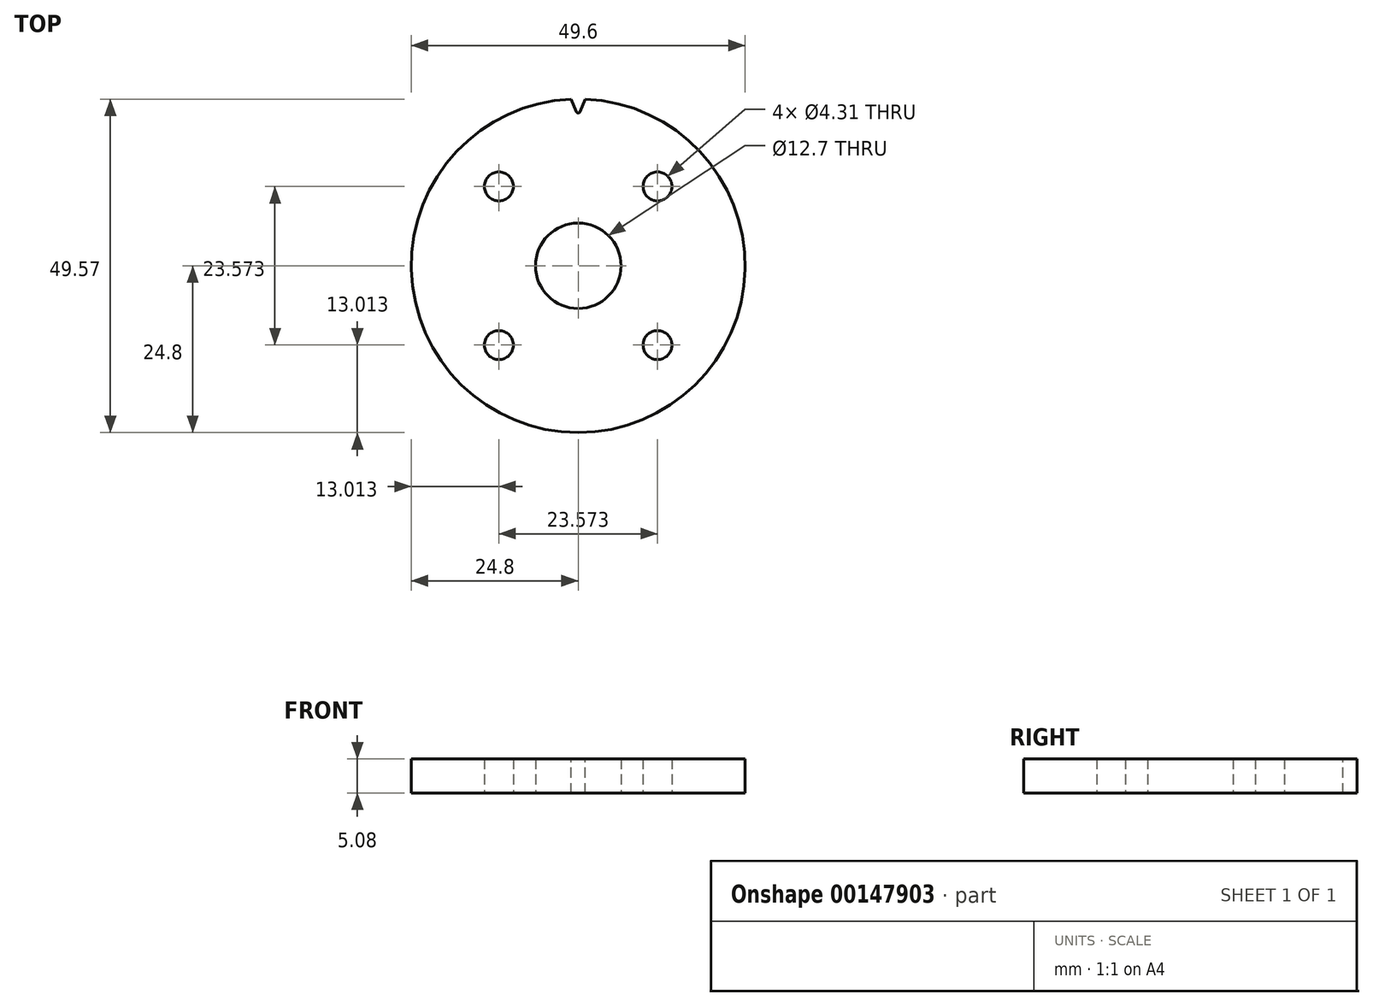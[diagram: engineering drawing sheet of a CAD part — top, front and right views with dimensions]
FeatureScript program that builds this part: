
annotation { "Feature Type Name" : "Feature", "Feature Type Description" : "" }
export const myFeature = defineFeature(function(context is Context, id is Id, definition is map)
    precondition{}
    {
        {
            var Q0;
            Q0=qCreatedBy(makeId("Top.planeOp"),FACE);
            var sketch = newSketch(context, id + "F0", { "sketchPlane" : qUnion([Q0])});
            skCircle(sketch, "E0", {"center": v(0, 0) * mm, "radius": 24.8 * mm});
            skCircle(sketch, "E1", {"center": v(0, 0) * mm, "radius": 11.11 * mm, "construction": true});
            skLineSegment(sketch, "E2.bottom", {"start": v(11.79, 11.79) * mm, "end": v(-11.79, 11.79) * mm, "construction": true});
            skLineSegment(sketch, "E2.top", {"start": v(11.79, -11.79) * mm, "end": v(-11.79, -11.79) * mm, "construction": true});
            skLineSegment(sketch, "E2.left", {"start": v(11.79, 11.79) * mm, "end": v(11.79, -11.79) * mm, "construction": true});
            skLineSegment(sketch, "E2.right", {"start": v(-11.79, 11.79) * mm, "end": v(-11.79, -11.79) * mm, "construction": true});
            skCircle(sketch, "E3", {"center": v(11.79, 11.79) * mm, "radius": 5.56 * mm, "construction": true});
            skCircle(sketch, "E4", {"center": v(-11.79, 11.79) * mm, "radius": 2.15 * mm});
            skCircle(sketch, "E5", {"center": v(11.79, 11.79) * mm, "radius": 2.15 * mm});
            skCircle(sketch, "E6", {"center": v(11.79, -11.79) * mm, "radius": 2.15 * mm});
            skCircle(sketch, "E7", {"center": v(-11.79, -11.79) * mm, "radius": 2.15 * mm});
            skCircle(sketch, "E8", {"center": v(0, 0) * mm, "radius": 6.35 * mm});
            skSolve(sketch);
        }
        {
            var Q0;
            Q0=makeQuery(id+"F0.imprint","IMPRINT",FACE,{"disambiguationData":[TD([[makeQuery(id+"F0.imprint","IMPRINT",EDGE,{"derivedFrom":sQuery(id+"F0.wireOp",EDGE,"d7zeTPih-CRss-xDOh-gPdP-rmPCdwzH7cdN.left")}),1.0]])]});
            var Q1;
            Q1=makeQuery(id+"F0.imprint","IMPRINT",FACE,{"disambiguationData":[TD([[makeQuery(id+"F0.imprint","IMPRINT",EDGE,{"derivedFrom":sQuery(id+"F0.wireOp",EDGE,"E0")}),1.0]])]});
            extrude(context, id + "F1", {"entities" : qUnion([Q0, Q1]), "depth" : 5.08 * mm});
        }
        {
            var Q0;
            Q0=makeQuery(id+"F1.opExtrude","CAP_FACE",FACE,{"disambiguationData":[OSD([sQuery(id+"F0.wireOp",EDGE,"d7zeTPih-CRss-xDOh-gPdP-rmPCdwzH7cdN.left"),sQuery(id+"F0.wireOp",EDGE,"d7zeTPih-CRss-xDOh-gPdP-rmPCdwzH7cdN.right"),sQuery(id+"F0.wireOp",EDGE,"ScfBMfkV-s1yN-Ls9R-SGr5-fEyGpD6zak8e"),sQuery(id+"F0.wireOp",EDGE,"xnxmVwjl-FvSF-m7sj-be2U-u85gZZGoORGZ"),sQuery(id+"F0.wireOp",EDGE,"E0")])],"isStart":false});
            var sketch = newSketch(context, id + "F2", { "sketchPlane" : qUnion([Q0])});
            skLineSegment(sketch, "E9", {"start": v(0, 0) * mm, "end": v(0, 24.8) * mm, "construction": true});
            skLineSegment(sketch, "E10", {"start": v(0, 0) * mm, "end": v(0.68, 24.79) * mm, "construction": true});
            skArc(sketch, "E11", {"start": v(1.03, 24.77) * mm, "mid": v(0, 24.8) * mm, "end": v(-1.03, 24.77) * mm});
            skLineSegment(sketch, "E12", {"start": v(-1.03, 24.77) * mm, "end": v(-0.28, 22.88) * mm});
            skLineSegment(sketch, "E13", {"start": v(1.03, 24.77) * mm, "end": v(0.28, 22.88) * mm});
            skPoint(sketch, "E14", {"position": v(0.65, 23.83) * mm});
            skArc(sketch, "E15", {"start": v(-0.28, 22.88) * mm, "mid": v(0, 22.7) * mm, "end": v(0.28, 22.88) * mm});
            skSolve(sketch);
        }
        {
            var Q0;
            Q0=qSketchRegion(id+"F2",true);
            var Q1;
            Q1=makeQuery(id+"F1.opExtrude","CAP_FACE",FACE,{"disambiguationData":[OSD([sQuery(id+"F0.wireOp",EDGE,"d7zeTPih-CRss-xDOh-gPdP-rmPCdwzH7cdN.left"),sQuery(id+"F0.wireOp",EDGE,"d7zeTPih-CRss-xDOh-gPdP-rmPCdwzH7cdN.right"),sQuery(id+"F0.wireOp",EDGE,"ScfBMfkV-s1yN-Ls9R-SGr5-fEyGpD6zak8e"),sQuery(id+"F0.wireOp",EDGE,"xnxmVwjl-FvSF-m7sj-be2U-u85gZZGoORGZ"),sQuery(id+"F0.wireOp",EDGE,"E0")])],"isStart":true});
            extrude(context, id + "F3", {"entities" : qUnion([Q0]), "operationType" : NewBodyOperationType.REMOVE, "endBound" : BoundingType.UP_TO_SURFACE, "oppositeDirection" : true, "endBoundEntityFace" : qUnion([Q1]), "depth" : 25.4 * mm});
        }
    });
